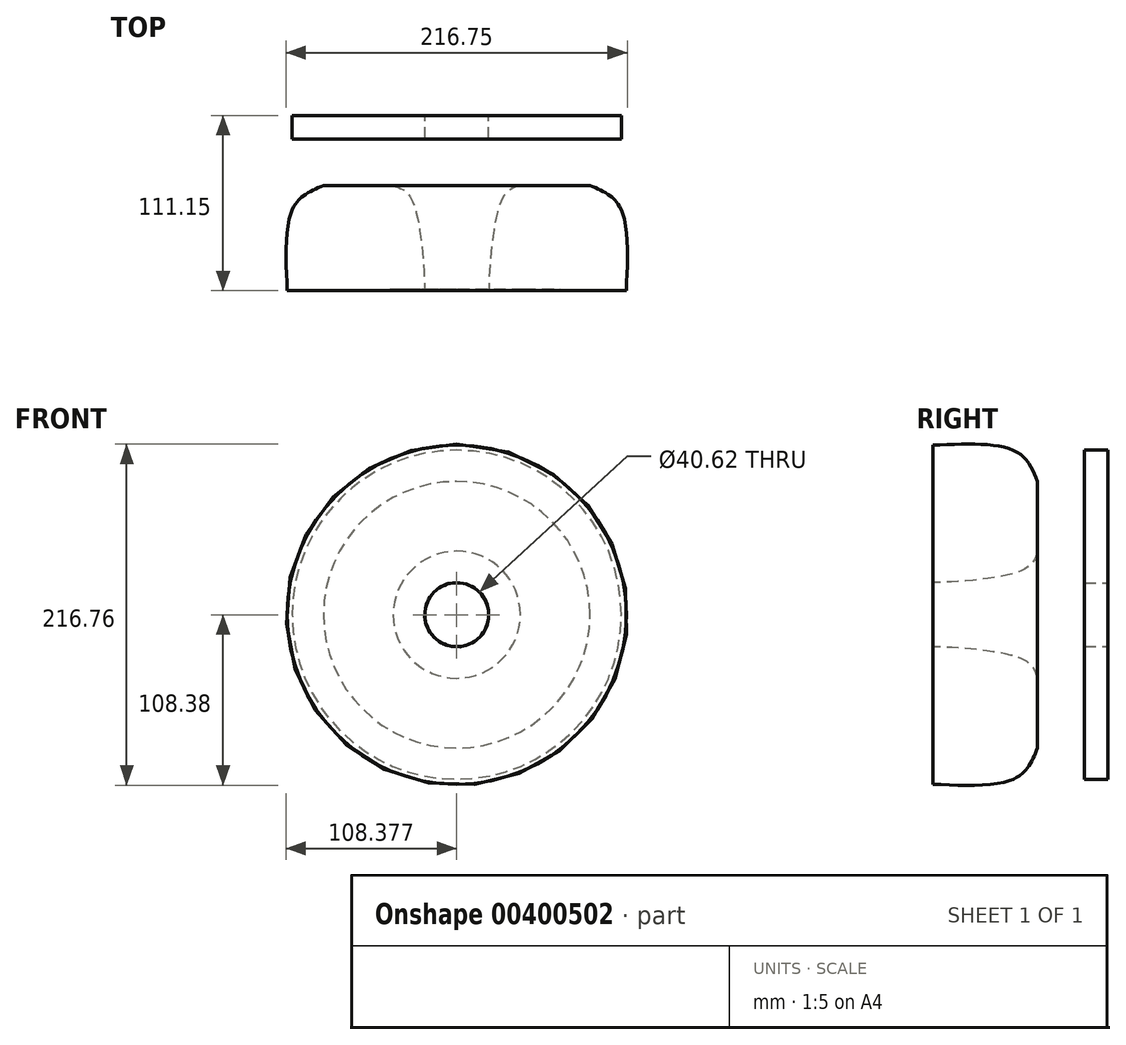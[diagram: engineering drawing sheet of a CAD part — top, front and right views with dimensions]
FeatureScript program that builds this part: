
annotation { "Feature Type Name" : "Feature", "Feature Type Description" : "" }
export const myFeature = defineFeature(function(context is Context, id is Id, definition is map)
    precondition{}
    {
        {
            var Q0;
            Q0=qCreatedBy(makeId("Top.planeOp"),FACE);
            var sketch = newSketch(context, id + "F0", { "sketchPlane" : qUnion([Q0])});
            skLineSegment(sketch, "E0.bottom", {"start": v(-37.2, 47.96) * mm, "end": v(46.98, 47.96) * mm});
            skLineSegment(sketch, "E0.top", {"start": v(-37.2, 33.03) * mm, "end": v(46.98, 33.03) * mm});
            skLineSegment(sketch, "E0.left", {"start": v(-37.2, 47.96) * mm, "end": v(-37.2, 33.03) * mm});
            skLineSegment(sketch, "E0.right", {"start": v(46.98, 47.96) * mm, "end": v(46.98, 33.03) * mm});
            skLineSegment(sketch, "E1.bottom", {"start": v(-31.8, 33.03) * mm, "end": v(41.84, 33.03) * mm});
            skLineSegment(sketch, "E1.top", {"start": v(-31.8, 18.84) * mm, "end": v(41.84, 18.84) * mm});
            skLineSegment(sketch, "E1.left", {"start": v(-31.8, 33.03) * mm, "end": v(-31.8, 18.84) * mm});
            skLineSegment(sketch, "E1.right", {"start": v(41.84, 33.03) * mm, "end": v(41.84, 18.84) * mm});
            skLineSegment(sketch, "E2.bottom", {"start": v(-24.71, 18.84) * mm, "end": v(35.23, 18.84) * mm});
            skLineSegment(sketch, "E2.top", {"start": v(-24.71, 3.43) * mm, "end": v(35.23, 3.43) * mm});
            skLineSegment(sketch, "E2.left", {"start": v(-24.71, 18.84) * mm, "end": v(-24.71, 3.43) * mm});
            skLineSegment(sketch, "E2.right", {"start": v(35.23, 18.84) * mm, "end": v(35.23, 3.43) * mm});
            skFitSpline(sketch, "E3", {"points": [v(-17.37, 3.43) * mm, v(-35.97, -9.54) * mm, v(-40.37, -63.13) * mm], "startDerivative": vector(-55.1, -22.02) * mm, "endDerivative": vector(4.85, -105.19) * mm});
            skFitSpline(sketch, "E4", {"points": [v(26.91, 3.43) * mm, v(39.64, -7.59) * mm, v(46.73, -63.13) * mm, v(46.49, -63.13) * mm, v(-40.37, -63.13) * mm], "startDerivative": vector(73.43, -20.72) * mm, "endDerivative": vector(-288.91, -3.33) * mm});
            skLineSegment(sketch, "E5", {"start": v(67.29, 63.86) * mm, "end": v(67.29, -69.73) * mm});
            skSolve(sketch);
        }
        {
            var Q0;
            Q0=makeQuery(id+"F0.imprint","IMPRINT",FACE,{"disambiguationData":[TD([[makeQuery(id+"F0.imprint","IMPRINT",EDGE,{"derivedFrom":sQuery(id+"F0.wireOp",EDGE,"E0.bottom")}),-1.0]])]});
            var Q1;
            {var subQ0=sQuery(id+"F0.wireOp",EDGE,"E3");Q1=makeQuery(id+"F0.imprint","IMPRINT",FACE,{"disambiguationData":[TD([[makeQuery(id+"F0.imprint","IMPRINT",EDGE,{"derivedFrom":subQ0}),1.0]])]});}
            var Q2;
            Q2=makeQuery(id+"F0.imprint","IMPRINT",FACE,{"disambiguationData":[TD([[makeQuery(id+"F0.imprint","IMPRINT",EDGE,{"derivedFrom":sQuery(id+"F0.wireOp",EDGE,"E1.bottom")}),-1.0]])]});
            var Q3;
            Q3=makeQuery(id+"F0.imprint","IMPRINT",FACE,{"disambiguationData":[TD([[makeQuery(id+"F0.imprint","IMPRINT",EDGE,{"derivedFrom":sQuery(id+"F0.wireOp",EDGE,"E2.bottom")}),-1.0]])]});
            var Q4;
            Q4=sQuery(id+"F0.wireOp",EDGE,"E5");
            revolve(context, id + "F1", {"entities" : qUnion([Q0, Q1, Q2, Q3]), "axis" : qUnion([Q4]), "revolveType" : RevolveType.FULL});
        }
    });
